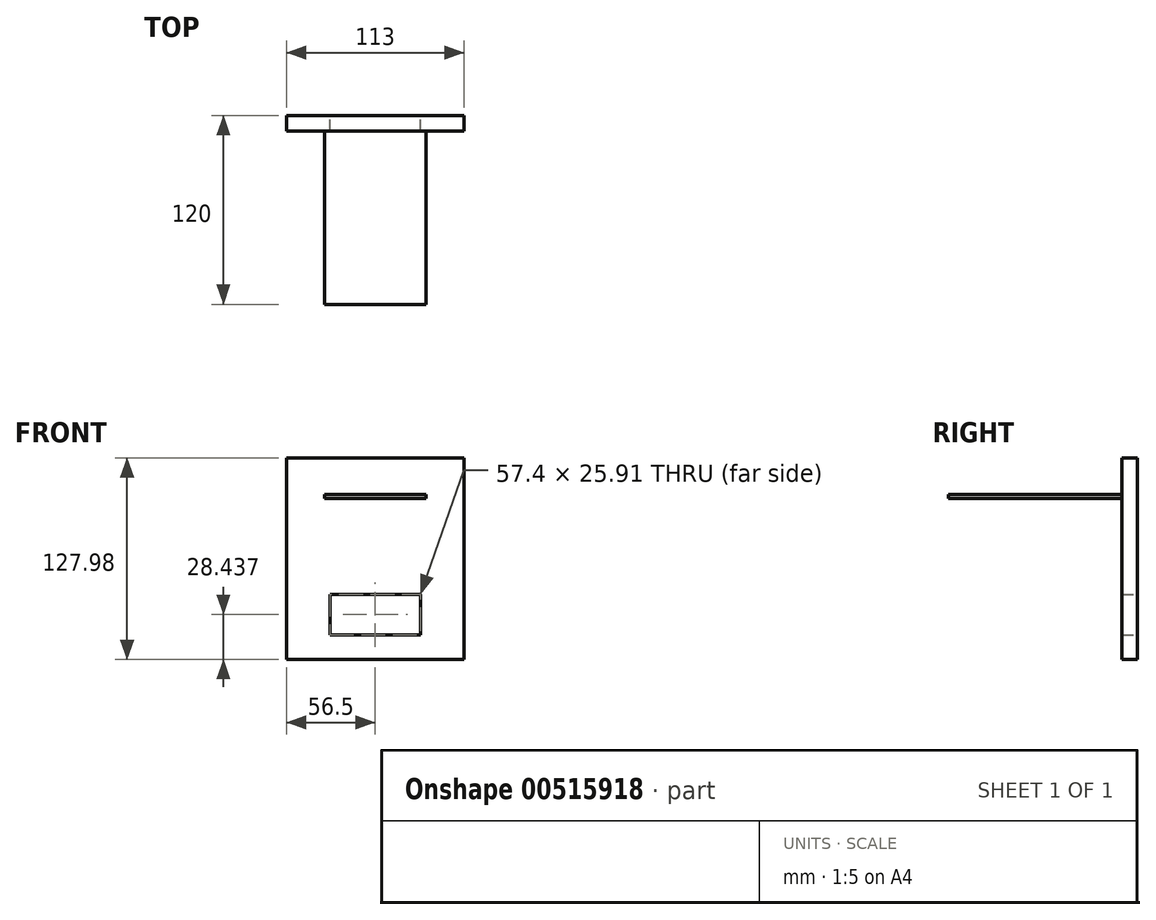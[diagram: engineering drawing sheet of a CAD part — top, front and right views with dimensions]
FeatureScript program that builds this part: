
annotation { "Feature Type Name" : "Feature", "Feature Type Description" : "" }
export const myFeature = defineFeature(function(context is Context, id is Id, definition is map)
    precondition{}
    {
        {
            var Q0;
            Q0=qCreatedBy(makeId("Front.planeOp"),FACE);
            var sketch = newSketch(context, id + "F0", { "sketchPlane" : qUnion([Q0])});
            skLineSegment(sketch, "E0.bottom", {"start": v(32.32, 58.25) * mm, "end": v(-32.32, 58.25) * mm});
            skLineSegment(sketch, "E0.top", {"start": v(32.32, 55.77) * mm, "end": v(-32.32, 55.77) * mm});
            skLineSegment(sketch, "E0.left", {"start": v(32.32, 58.25) * mm, "end": v(32.32, 55.77) * mm});
            skLineSegment(sketch, "E0.right", {"start": v(-32.32, 58.25) * mm, "end": v(-32.32, 55.77) * mm});
            skPoint(sketch, "E0.middle", {"position": v(0, 57.01) * mm});
            skSolve(sketch);
        }
        {
            var Q0;
            Q0 = qSketchRegion(id + "F0", true);
            extrude(context, id + "F1", {"entities" : qUnion([Q0]), "depth" : 120 * mm, "offsetDistance" : 25 * mm});
        }
        {
            var Q0;
            Q0=qCreatedBy(makeId("Front.planeOp"),FACE);
            var sketch = newSketch(context, id + "F2", { "sketchPlane" : qUnion([Q0])});
            skLineSegment(sketch, "E1.bottom", {"start": v(56.5, -46.54) * mm, "end": v(-56.5, -46.54) * mm});
            skLineSegment(sketch, "E1.top", {"start": v(56.5, 81.44) * mm, "end": v(-56.5, 81.44) * mm});
            skLineSegment(sketch, "E1.left", {"start": v(56.5, -46.54) * mm, "end": v(56.5, 81.44) * mm});
            skLineSegment(sketch, "E1.right", {"start": v(-56.5, -46.54) * mm, "end": v(-56.5, 81.44) * mm});
            skPoint(sketch, "E1.middle", {"position": v(0, 17.45) * mm});
            skSolve(sketch);
        }
        {
            var Q0;
            Q0 = qSketchRegion(id + "F2", true);
            extrude(context, id + "F3", {"entities" : qUnion([Q0]), "operationType" : NewBodyOperationType.ADD, "depth" : 10 * mm, "offsetDistance" : 25 * mm});
        }
        {
            var Q0;
            Q0=makeQuery(id+"F3.boolean.opBoolean","MERGE",FACE,{"derivedFrom":[makeQuery(id+"F1.opExtrude","CAP_FACE",FACE,{"disambiguationData":[OSD([sQuery(id+"F0.wireOp",EDGE,"E0.bottom"),sQuery(id+"F0.wireOp",EDGE,"E0.top"),sQuery(id+"F0.wireOp",EDGE,"E0.left"),sQuery(id+"F0.wireOp",EDGE,"E0.right")])],"isStart":true}),makeQuery(id+"F3.opExtrude","CAP_FACE",FACE,{"disambiguationData":[OSD([sQuery(id+"F2.wireOp",EDGE,"E1.bottom"),sQuery(id+"F2.wireOp",EDGE,"E1.top"),sQuery(id+"F2.wireOp",EDGE,"E1.left"),sQuery(id+"F2.wireOp",EDGE,"E1.right")])],"isStart":true})]});
            var sketch = newSketch(context, id + "F4", { "sketchPlane" : qUnion([Q0])});
            skLineSegment(sketch, "E2.bottom", {"start": v(28.7, -31.06) * mm, "end": v(-28.7, -31.06) * mm});
            skLineSegment(sketch, "E2.top", {"start": v(28.7, -5.15) * mm, "end": v(-28.7, -5.15) * mm});
            skLineSegment(sketch, "E2.left", {"start": v(28.7, -31.06) * mm, "end": v(28.7, -5.15) * mm});
            skLineSegment(sketch, "E2.right", {"start": v(-28.7, -31.06) * mm, "end": v(-28.7, -5.15) * mm});
            skPoint(sketch, "E2.middle", {"position": v(0, -18.1) * mm});
            skSolve(sketch);
        }
        {
            var Q0;
            Q0 = qSketchRegion(id + "F4", true);
            extrude(context, id + "F5", {"entities" : qUnion([Q0]), "operationType" : NewBodyOperationType.REMOVE, "oppositeDirection" : true, "depth" : 25 * mm, "offsetDistance" : 25 * mm});
        }
    });
